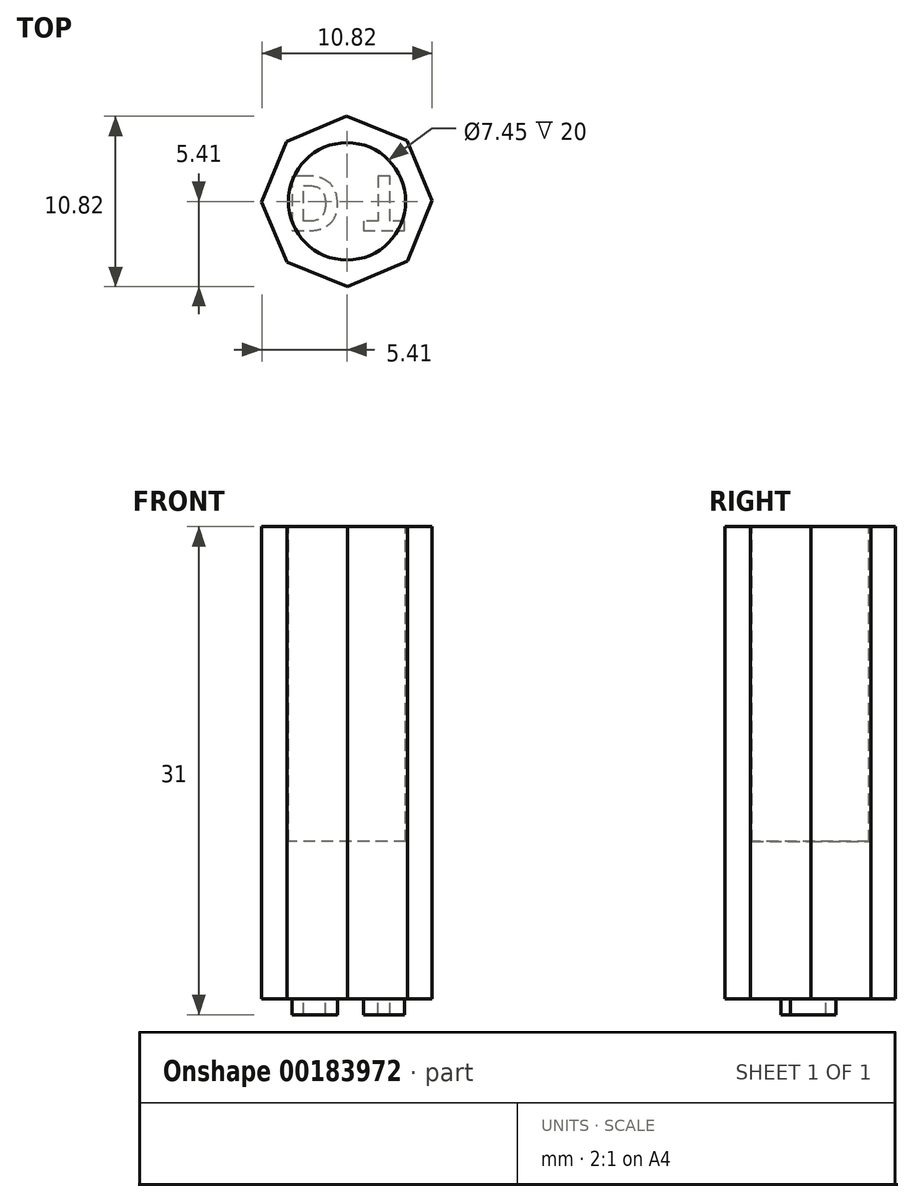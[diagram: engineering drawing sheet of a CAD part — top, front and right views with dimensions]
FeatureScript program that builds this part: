
annotation { "Feature Type Name" : "Feature", "Feature Type Description" : "" }
export const myFeature = defineFeature(function(context is Context, id is Id, definition is map)
    precondition{}
    {
        {
            var Q0;
            Q0=qCreatedBy(makeId("Top.planeOp"),FACE);
            var sketch = newSketch(context, id + "F0", { "sketchPlane" : qUnion([Q0])});
            skCircle(sketch, "E0.cCircle", {"center": v(0, 0) * mm, "radius": 5 * mm, "construction": true});
            skLineSegment(sketch, "E0.0", {"start": v(-3.86, 3.8) * mm, "end": v(-0.04, 5.41) * mm});
            skLineSegment(sketch, "E0.1", {"start": v(-0.04, 5.41) * mm, "end": v(3.8, 3.86) * mm});
            skLineSegment(sketch, "E0.2", {"start": v(3.8, 3.86) * mm, "end": v(5.41, 0.04) * mm});
            skLineSegment(sketch, "E0.3", {"start": v(5.41, 0.04) * mm, "end": v(3.86, -3.8) * mm});
            skLineSegment(sketch, "E0.4", {"start": v(3.86, -3.8) * mm, "end": v(0.04, -5.41) * mm});
            skLineSegment(sketch, "E0.5", {"start": v(0.04, -5.41) * mm, "end": v(-3.8, -3.86) * mm});
            skLineSegment(sketch, "E0.6", {"start": v(-3.8, -3.86) * mm, "end": v(-5.41, -0.04) * mm});
            skLineSegment(sketch, "E0.7", {"start": v(-5.41, -0.04) * mm, "end": v(-3.86, 3.8) * mm});
            skPoint(sketch, "E0.0.midPoint", {"position": v(-1.95, 4.6) * mm});
            skSolve(sketch);
        }
        {
            var Q0;
            Q0=makeQuery(id+"F0.imprint","IMPRINT",FACE,{"disambiguationData":[TD([[makeQuery(id+"F0.imprint","IMPRINT",EDGE,{"derivedFrom":sQuery(id+"F0.wireOp",EDGE,"E0.0")}),-1.0]])]});
            extrude(context, id + "F1", {"entities" : qUnion([Q0]), "depth" : 30 * mm});
        }
        {
            var Q0;
            Q0=makeQuery(id+"F1.opExtrude","CAP_FACE",FACE,{"disambiguationData":[OSD([sQuery(id+"F0.wireOp",EDGE,"E0.0"),sQuery(id+"F0.wireOp",EDGE,"E0.1"),sQuery(id+"F0.wireOp",EDGE,"E0.2"),sQuery(id+"F0.wireOp",EDGE,"E0.3"),sQuery(id+"F0.wireOp",EDGE,"E0.4"),sQuery(id+"F0.wireOp",EDGE,"E0.5"),sQuery(id+"F0.wireOp",EDGE,"E0.6"),sQuery(id+"F0.wireOp",EDGE,"E0.7")])],"isStart":false});
            var sketch = newSketch(context, id + "F2", { "sketchPlane" : qUnion([Q0])});
            skCircle(sketch, "E1", {"center": v(0, 0) * mm, "radius": 3.73 * mm});
            skSolve(sketch);
        }
        {
            var Q0;
            Q0=makeQuery(id+"F2.imprint","IMPRINT",FACE,{"disambiguationData":[TD([[makeQuery(id+"F2.imprint","IMPRINT",EDGE,{"derivedFrom":sQuery(id+"F2.wireOp",EDGE,"E1")}),1.0]])]});
            extrude(context, id + "F3", {"entities" : qUnion([Q0]), "operationType" : NewBodyOperationType.REMOVE, "oppositeDirection" : true, "depth" : 20 * mm});
        }
        {
            var Q0;
            Q0=makeQuery(id+"F1.opExtrude","CAP_FACE",FACE,{"disambiguationData":[OSD([sQuery(id+"F0.wireOp",EDGE,"E0.0"),sQuery(id+"F0.wireOp",EDGE,"E0.1"),sQuery(id+"F0.wireOp",EDGE,"E0.2"),sQuery(id+"F0.wireOp",EDGE,"E0.3"),sQuery(id+"F0.wireOp",EDGE,"E0.4"),sQuery(id+"F0.wireOp",EDGE,"E0.5"),sQuery(id+"F0.wireOp",EDGE,"E0.6"),sQuery(id+"F0.wireOp",EDGE,"E0.7")])],"isStart":true});
            var sketch = newSketch(context, id + "F4", { "sketchPlane" : qUnion([Q0])});
            skText(sketch, "E2", { "text": "D T", "fontName": "OpenSans-Bold.ttf"});
            const initialGuessF4  = {"E2": [-0.00392, -0.00161, 1, 0, 0.0035]};
            skSetInitialGuess(sketch, initialGuessF4);
            skSolve(sketch);
        }
        {
            var Q0;
            Q0 = qSketchRegion(id + "F4", true);
            extrude(context, id + "F5", {"entities" : qUnion([Q0]), "operationType" : NewBodyOperationType.ADD, "depth" : 1 * mm});
        }
    });
